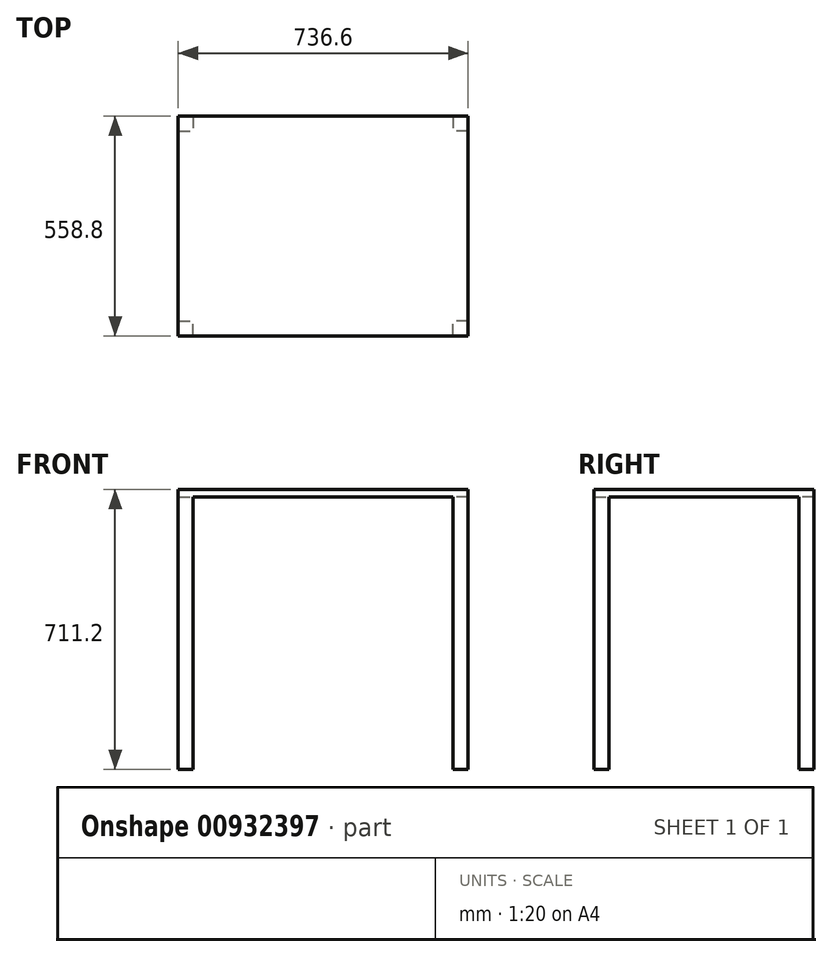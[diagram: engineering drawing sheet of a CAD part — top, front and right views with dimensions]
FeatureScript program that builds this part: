
annotation { "Feature Type Name" : "Feature", "Feature Type Description" : "" }
export const myFeature = defineFeature(function(context is Context, id is Id, definition is map)
    precondition{}
    {
        {
            var Q0;
            Q0=qCreatedBy(makeId("Top.planeOp"),FACE);
            cPlane(context, id + "F0", {"entities" : qUnion([Q0]), "cplaneType" : CPlaneType.OFFSET, "offset" : 711.2 * mm, "width" : 152.4 * mm, "height" : 152.4 * mm});
        }
        {
            var Q0;
            Q0=qCreatedBy(id+"F0.planeOp",FACE);
            var sketch = newSketch(context, id + "F1", { "sketchPlane" : qUnion([Q0])});
            skLineSegment(sketch, "E0.bottom", {"start": v(368.3, -279.4) * mm, "end": v(-368.3, -279.4) * mm});
            skLineSegment(sketch, "E0.top", {"start": v(368.3, 279.4) * mm, "end": v(-368.3, 279.4) * mm});
            skLineSegment(sketch, "E0.left", {"start": v(368.3, -279.4) * mm, "end": v(368.3, 279.4) * mm});
            skLineSegment(sketch, "E0.right", {"start": v(-368.3, -279.4) * mm, "end": v(-368.3, 279.4) * mm});
            skPoint(sketch, "E0.middle", {"position": v(0, 0) * mm});
            skSolve(sketch);
        }
        {
            var Q0;
            Q0 = qSketchRegion(id + "F1", true);
            extrude(context, id + "F2", {"entities" : qUnion([Q0]), "oppositeDirection" : true, "depth" : 19.05 * mm, "offsetDistance" : 25.4 * mm});
        }
        {
            var Q0;
            Q0=makeQuery(id+"F2.opExtrude","CAP_FACE",FACE,{"disambiguationData":[OSD([sQuery(id+"F1.wireOp",EDGE,"E0.bottom"),sQuery(id+"F1.wireOp",EDGE,"E0.top"),sQuery(id+"F1.wireOp",EDGE,"E0.left"),sQuery(id+"F1.wireOp",EDGE,"E0.right")])],"isStart":false});
            var sketch = newSketch(context, id + "F3", { "sketchPlane" : qUnion([Q0])});
            skLineSegment(sketch, "E1.bottom", {"start": v(-368.3, 279.4) * mm, "end": v(-330.2, 279.4) * mm});
            skLineSegment(sketch, "E1.top", {"start": v(-368.3, 241.3) * mm, "end": v(-330.2, 241.3) * mm});
            skLineSegment(sketch, "E1.left", {"start": v(-368.3, 279.4) * mm, "end": v(-368.3, 241.3) * mm});
            skLineSegment(sketch, "E1.right", {"start": v(-330.2, 279.4) * mm, "end": v(-330.2, 241.3) * mm});
            skLineSegment(sketch, "E2", {"start": v(0, 279.4) * mm, "end": v(0, 0) * mm, "construction": true});
            skLineSegment(sketch, "E3", {"start": v(0, 0) * mm, "end": v(368.3, 0) * mm, "construction": true});
            skLineSegment(sketch, "E4.MirrorCS", {"start": v(368.3, 279.4) * mm, "end": v(330.2, 279.4) * mm});
            skLineSegment(sketch, "E5.MirrorCS", {"start": v(368.3, 279.4) * mm, "end": v(368.3, 241.3) * mm});
            skLineSegment(sketch, "E6.MirrorCS", {"start": v(368.3, 241.3) * mm, "end": v(330.2, 241.3) * mm});
            skLineSegment(sketch, "E7.MirrorCS", {"start": v(330.2, 279.4) * mm, "end": v(330.2, 241.3) * mm});
            skLineSegment(sketch, "E8.MirrorCS", {"start": v(330.2, -279.4) * mm, "end": v(330.2, -241.3) * mm});
            skLineSegment(sketch, "E9.MirrorCS", {"start": v(368.3, -241.3) * mm, "end": v(330.2, -241.3) * mm});
            skLineSegment(sketch, "E10.MirrorCS", {"start": v(-330.2, -279.4) * mm, "end": v(-330.2, -241.3) * mm});
            skLineSegment(sketch, "E11.MirrorCS", {"start": v(-368.3, -241.3) * mm, "end": v(-330.2, -241.3) * mm});
            skLineSegment(sketch, "E12.MirrorCS", {"start": v(-368.3, -279.4) * mm, "end": v(-368.3, -241.3) * mm});
            skLineSegment(sketch, "E13.MirrorCS", {"start": v(-368.3, -279.4) * mm, "end": v(-330.2, -279.4) * mm});
            skLineSegment(sketch, "E14.MirrorCS", {"start": v(368.3, -279.4) * mm, "end": v(368.3, -241.3) * mm});
            skLineSegment(sketch, "E15.MirrorCS", {"start": v(368.3, -279.4) * mm, "end": v(330.2, -279.4) * mm});
            skSolve(sketch);
        }
        {
            var Q0;
            Q0 = qSketchRegion(id + "F3", true);
            var Q1;
            Q1=qCreatedBy(makeId("Top.planeOp"),FACE);
            extrude(context, id + "F4", {"entities" : qUnion([Q0]), "operationType" : NewBodyOperationType.ADD, "endBound" : BoundingType.UP_TO_SURFACE, "depth" : 25.4 * mm, "endBoundEntityFace" : qUnion([Q1]), "offsetDistance" : 25.4 * mm});
        }
    });
